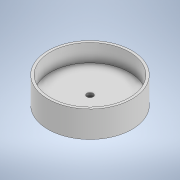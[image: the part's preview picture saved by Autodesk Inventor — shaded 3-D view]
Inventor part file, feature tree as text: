
AUTODESK INVENTOR PART (.ipt)
format: ipt  version: 2020 (Build 240168000, 168)  size: 116,736 bytes
history: native  units: mm
features: sketch x3, extrude x2, hole x1
ambient origin geometry x8: Origin, YZ Plane, XZ Plane, XY Plane, X Axis, Y Axis, Z Axis, Center Point
bodies: Solid1 (feature_tree)
feature tree (6):
  extrude  "Extrusion1"  Depth=9.0mm TaperAngle=0.0deg
  extrude  "Extrusion2"  Depth=18.0mm TaperAngle=0.0deg
  hole  "Hole1"  [1 undecoded]
  sketch  "Sketch1"  dims[d0=86.0mm d1=9.0mm d2=0.0mm]
  sketch  "Sketch2"  dims[d3=2.5mm d4=18.0mm d5=0.0mm]
  sketch  "Sketch3"  dims[d6=5.9mm d7=6.0mm d8=6.5mm d9=2.0mm d10=90.0deg d11=8.5mm d12=0.0mm]
note: 1 required parameter value undecoded (feature->parameter linkage not recoverable at this tier; creation-order binding heuristic only, values carry confidence <= 0.55)
